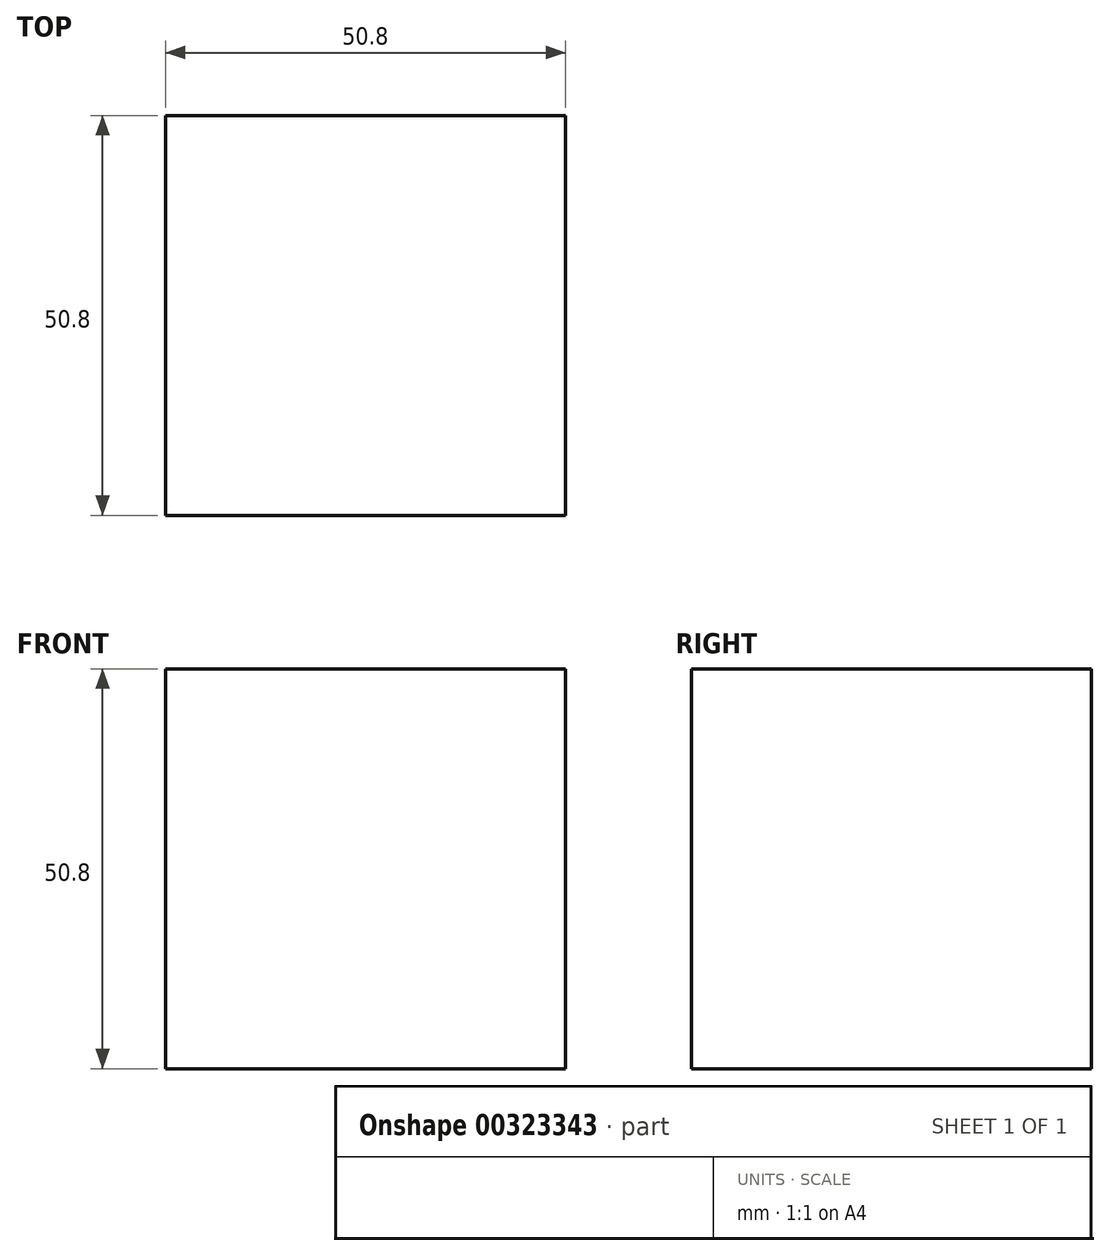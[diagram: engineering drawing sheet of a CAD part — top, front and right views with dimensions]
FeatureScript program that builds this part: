
annotation { "Feature Type Name" : "Feature", "Feature Type Description" : "" }
export const myFeature = defineFeature(function(context is Context, id is Id, definition is map)
    precondition{}
    {
        {
            var Q0;
            Q0=qCreatedBy(makeId("Front.planeOp"),FACE);
            var sketch = newSketch(context, id + "F0", { "sketchPlane" : qUnion([Q0])});
            skLineSegment(sketch, "E0.bottom", {"start": v(0, 0) * mm, "end": v(50.8, 0) * mm});
            skLineSegment(sketch, "E0.top", {"start": v(0, -50.8) * mm, "end": v(50.8, -50.8) * mm});
            skLineSegment(sketch, "E0.left", {"start": v(0, 0) * mm, "end": v(0, -50.8) * mm});
            skLineSegment(sketch, "E0.right", {"start": v(50.8, 0) * mm, "end": v(50.8, -50.8) * mm});
            skSolve(sketch);
        }
        {
            var Q0;
            Q0=makeQuery(id+"F0.imprint","IMPRINT",FACE,{"disambiguationData":[TD([[makeQuery(id+"F0.imprint","IMPRINT",EDGE,{"derivedFrom":sQuery(id+"F0.wireOp",EDGE,"E0.bottom")}),-1.0]])]});
            extrude(context, id + "F1", {"entities" : qUnion([Q0]), "depth" : 50.8 * mm});
        }
    });
